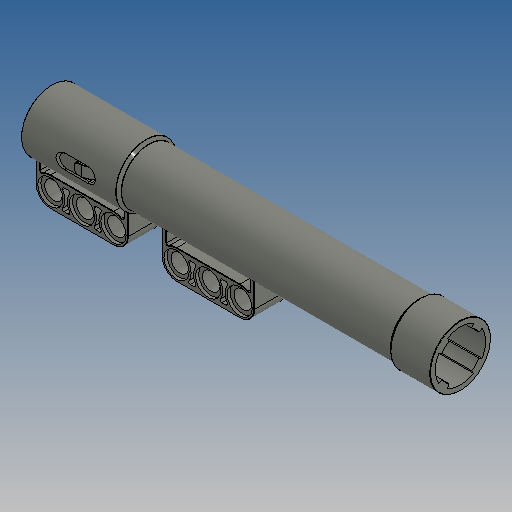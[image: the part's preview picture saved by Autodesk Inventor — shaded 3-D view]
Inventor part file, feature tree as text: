
AUTODESK INVENTOR PART (.ipt)
format: ipt  version: 2025 (Build 290162010, 162A)  size: 784,384 bytes
history: native  units: mm
features: sketch x13, extrude x12, mirror x3, fillet x3, revolve x2, pattern_circular x2, plane x2, pattern_linear x1, delete_face x1
ambient origin geometry x8: Origin, YZ Plane, XZ Plane, XY Plane, X Axis, Y Axis, Z Axis, Center Point
bodies: Volumenkörper1 (feature_tree), Volumenkörper2 (feature_tree)
feature tree (39):
  sketch  "Skizze1"  dims[d0=103.7mm d1=24.0mm]
  revolve  "Umdrehung1"
  extrude  "Extrusion1"  Depth=103.7mm
  pattern_circular  "Runde Anordnung1"  Angle=45.0deg  [1 undecoded]
  extrude  "Extrusion2"  TaperAngle=60.0deg  [1 undecoded]
  plane  "Arbeitsebene1"
  extrude  "Extrusion3"  Depth=80.0mm TaperAngle=0.0deg
  mirror  "Spiegeln1"
  extrude  "Extrusion4"  Depth=80.0mm TaperAngle=360.0deg
  extrude  "Extrusion5"  Depth=3.2mm
  extrude  "Extrusion6"  Depth=80.0mm
  extrude  "Extrusion7"  Depth=80.0mm
  extrude  "Extrusion8"  Depth=80.0mm
  pattern_linear  "Rechteckige Anordnung1"  Spacing1=0.0mm  [1 undecoded]
  delete_face  "Fläche löschen1"
  fillet  "Rundung1"  Radius=7.2mm
  mirror  "Spiegeln2"
  fillet  "Rundung2"  Radius=1.0mm
  extrude  "Extrusion12"  Depth=80.0mm
  revolve  "Umdrehung2"
  plane  "Arbeitsebene2"
  extrude  "Extrusion9"  Depth=80.0mm
  extrude  "Extrusion10"  Depth=80.0mm
  fillet  "Rundung3"  Radius=4.5mm
  mirror  "Spiegeln3"
  extrude  "Extrusion11"  Depth=4.0mm TaperAngle=0.0deg
  pattern_circular  "Runde Anordnung2"  [2 undecoded]
  sketch  "Skizze2"  dims[d2=10.0mm]
  sketch  "Skizze3"  dims[d3=45.0deg]
  sketch  "Skizze4"  dims[d4=15.4mm]
  sketch  "Skizze5"  dims[d5=14.0mm]
  sketch  "Skizze6"  dims[d6=11.0mm]
  sketch  "Skizze7"  dims[d7=360.0deg]
  sketch  "Skizze8"  dims[d8=3.0mm]
  sketch  "Skizze9"  dims[d9=13.8mm]
  sketch  "Skizze10"  dims[d10=12.8mm]
  sketch  "Skizze11"  dims[d11=1.3mm]
  sketch  "Skizze12"  dims[d12=1.3mm]
  sketch  "Skizze13"  dims[d13=45.0deg d14=45.0deg d15=60.0deg d16=9.0mm d17=0.0mm d18=40.0mm d19=360.0deg d21=3.2mm d22=13.0mm d23=5.3mm d24=9.0mm d25=0.0mm d26=0.0mm d27=7.2mm d28=1.0mm d29=45.0deg d30=7.4mm d31=16.0mm d32=12.0mm d33=4.5mm d34=4.0mm d35=0.0mm d36=6.4mm d37=0.8mm d38=0.0mm d39=0.4mm d40=1.1mm d41=3.6mm d42=0.0mm d43=1.1mm d45=3.2mm d46=0.0mm d47=0.4mm d48=0.0mm d49=0.5mm d50=20.0mm d52=32.0mm d53=0.4mm d54=0.1mm d55=13.4mm d56=6.4mm d57=0.4mm d58=360.0deg d59=10.9mm d60=1.0mm d61=16.0mm d62=7.5mm d63=2.8mm d64=4.9mm d65=13.1mm d66=10.0mm d67=0.0mm d68=3.490659mm d69=2.0mm d70=1.055514mm d71=0.0mm d72=0.0mm d73=0.1mm d74=4.8mm d75=1.6mm d76=0.0mm d77=0.0mm d78=40.0mm d79=360.0deg d81=2.2mm d82=12.4mm d83=80.0mm d84=0.0mm]
note: 5 required parameter values undecoded (feature->parameter linkage not recoverable at this tier; creation-order binding heuristic only, values carry confidence <= 0.55)
